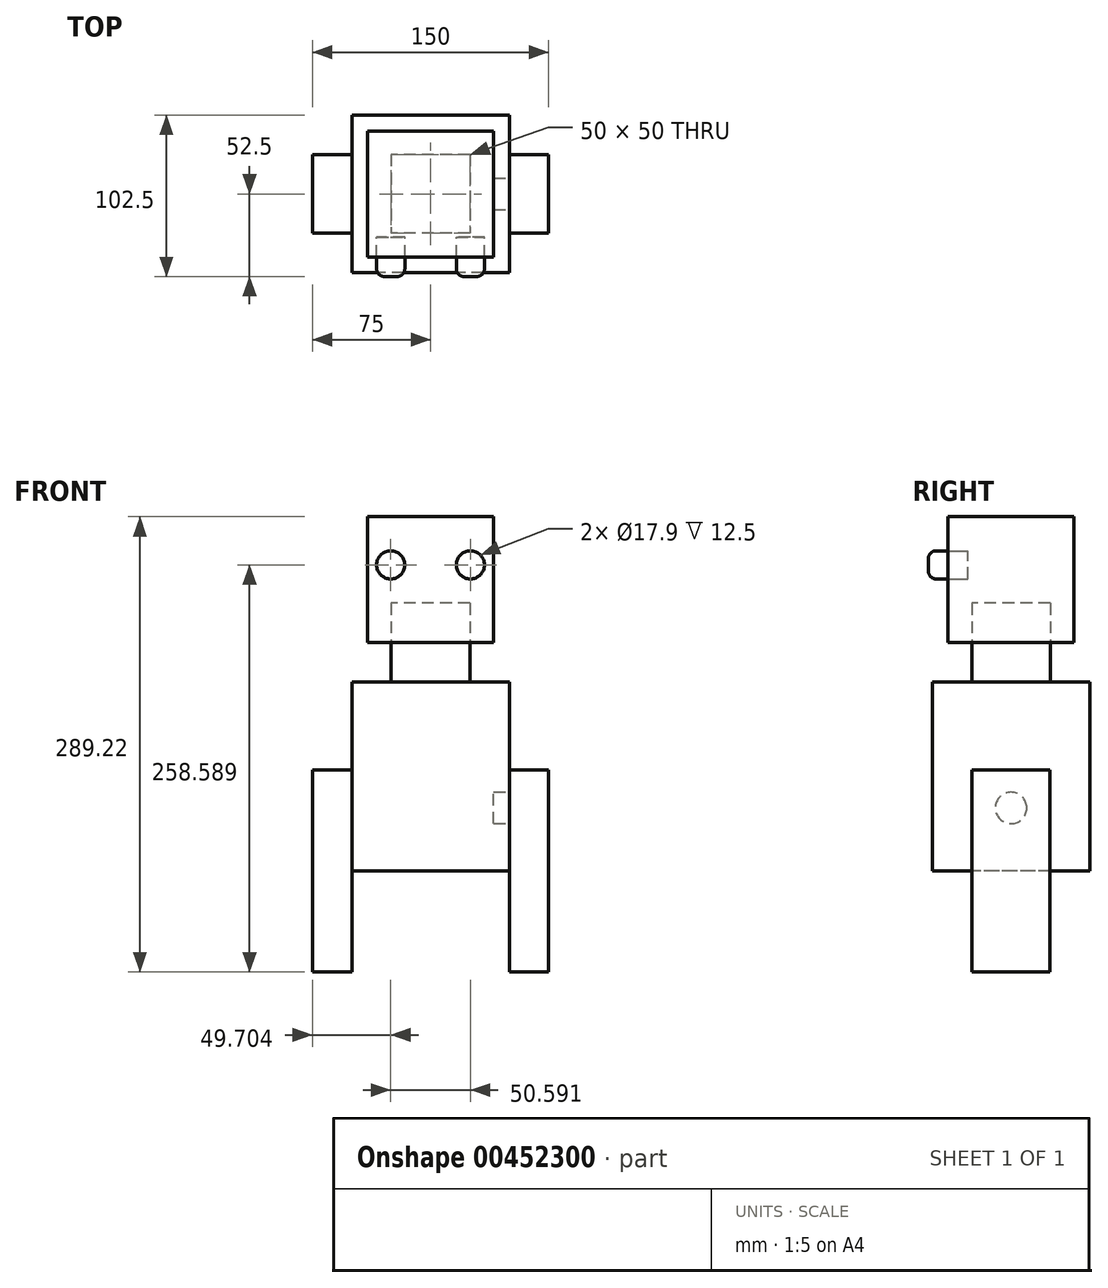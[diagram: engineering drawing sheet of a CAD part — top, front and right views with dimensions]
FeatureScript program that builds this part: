
annotation { "Feature Type Name" : "Feature", "Feature Type Description" : "" }
export const myFeature = defineFeature(function(context is Context, id is Id, definition is map)
    precondition{}
    {
        {
            var Q0;
            Q0=qCreatedBy(makeId("Top.planeOp"),FACE);
            var sketch = newSketch(context, id + "F0", { "sketchPlane" : qUnion([Q0])});
            skLineSegment(sketch, "E0.bottom", {"start": v(50, 50) * mm, "end": v(-50, 50) * mm});
            skLineSegment(sketch, "E0.top", {"start": v(50, -50) * mm, "end": v(-50, -50) * mm});
            skLineSegment(sketch, "E0.left", {"start": v(50, 50) * mm, "end": v(50, -50) * mm});
            skLineSegment(sketch, "E0.right", {"start": v(-50, 50) * mm, "end": v(-50, -50) * mm});
            skPoint(sketch, "E0.middle", {"position": v(0, 0) * mm});
            skSolve(sketch);
        }
        {
            var Q0;
            Q0=makeQuery(id+"F0.imprint","IMPRINT",FACE,{"disambiguationData":[TD([[makeQuery(id+"F0.imprint","IMPRINT",EDGE,{"derivedFrom":sQuery(id+"F0.wireOp",EDGE,"E0.bottom")}),1.0]])]});
            extrude(context, id + "F1", {"entities" : qUnion([Q0]), "depth" : 120 * mm});
        }
        {
            var Q0;
            Q0=makeQuery(id+"F1.opExtrude","CAP_FACE",FACE,{"disambiguationData":[OSD([sQuery(id+"F0.wireOp",EDGE,"E0.bottom"),sQuery(id+"F0.wireOp",EDGE,"E0.top"),sQuery(id+"F0.wireOp",EDGE,"E0.left"),sQuery(id+"F0.wireOp",EDGE,"E0.right")])],"isStart":false});
            var sketch = newSketch(context, id + "F2", { "sketchPlane" : qUnion([Q0])});
            skLineSegment(sketch, "E1.bottom", {"start": v(25, 25) * mm, "end": v(-25, 25) * mm});
            skLineSegment(sketch, "E1.top", {"start": v(25, -25) * mm, "end": v(-25, -25) * mm});
            skLineSegment(sketch, "E1.left", {"start": v(25, 25) * mm, "end": v(25, -25) * mm});
            skLineSegment(sketch, "E1.right", {"start": v(-25, 25) * mm, "end": v(-25, -25) * mm});
            skPoint(sketch, "E1.middle", {"position": v(0, 0) * mm});
            skSolve(sketch);
        }
        {
            var Q0;
            Q0=makeQuery(id+"F2.imprint","IMPRINT",FACE,{"disambiguationData":[TD([[makeQuery(id+"F2.imprint","IMPRINT",EDGE,{"derivedFrom":sQuery(id+"F2.wireOp",EDGE,"E1.bottom")}),1.0]])]});
            extrude(context, id + "F3", {"entities" : qUnion([Q0]), "operationType" : NewBodyOperationType.ADD, "depth" : 50 * mm});
        }
        {
            var Q0;
            Q0=qCreatedBy(makeId("Top.planeOp"),FACE);
            cPlane(context, id + "F4", {"entities" : qUnion([Q0]), "cplaneType" : CPlaneType.OFFSET, "offset" : 145 * mm, "width" : 150 * mm, "height" : 150 * mm});
        }
        {
            var Q0;
            Q0=qCreatedBy(id+"F4.planeOp",FACE);
            var sketch = newSketch(context, id + "F5", { "sketchPlane" : qUnion([Q0])});
            skLineSegment(sketch, "E2.bottom", {"start": v(-40, -40) * mm, "end": v(40, -40) * mm});
            skLineSegment(sketch, "E2.top", {"start": v(-40, 40) * mm, "end": v(40, 40) * mm});
            skLineSegment(sketch, "E2.left", {"start": v(-40, -40) * mm, "end": v(-40, 40) * mm});
            skLineSegment(sketch, "E2.right", {"start": v(40, -40) * mm, "end": v(40, 40) * mm});
            skPoint(sketch, "E2.middle", {"position": v(0, 0) * mm});
            skSolve(sketch);
        }
        {
            var Q0;
            Q0=makeQuery(id+"F5.imprint","IMPRINT",FACE,{"disambiguationData":[TD([[makeQuery(id+"F5.imprint","IMPRINT",EDGE,{"derivedFrom":sQuery(id+"F5.wireOp",EDGE,"E2.bottom")}),1.0]])]});
            extrude(context, id + "F6", {"entities" : qUnion([Q0]), "depth" : 80 * mm});
        }
        {
            var Q0;
            Q0=makeQuery(id+"F1.opExtrude","SWEPT_BODY",BODY,{"disambiguationData":[OSD([sQuery(id+"F0.wireOp",EDGE,"E0.bottom"),sQuery(id+"F0.wireOp",EDGE,"E0.top"),sQuery(id+"F0.wireOp",EDGE,"E0.left"),sQuery(id+"F0.wireOp",EDGE,"E0.right")])]});
            var Q1;
            Q1=makeQuery(id+"F6.opExtrude","SWEPT_BODY",BODY,{"disambiguationData":[OSD([sQuery(id+"F5.wireOp",EDGE,"E2.bottom"),sQuery(id+"F5.wireOp",EDGE,"E2.top"),sQuery(id+"F5.wireOp",EDGE,"E2.left"),sQuery(id+"F5.wireOp",EDGE,"E2.right")])]});
            booleanBodies(context, id + "F7", {"operationType" : BooleanOperationType.SUBTRACTION, "tools" : qUnion([Q0]), "targets" : qUnion([Q1]), "keepTools" : true});
        }
        {
            var Q0;
            Q0=makeQuery(id+"F1.opExtrude","SWEPT_FACE",FACE,{"disambiguationData":[OSD([sQuery(id+"F0.wireOp",EDGE,"E0.left")])]});
            var sketch = newSketch(context, id + "F8", { "sketchPlane" : qUnion([Q0])});
            skLineSegment(sketch, "E3", {"start": v(0, 0) * mm, "end": v(0, 40) * mm});
            skCircle(sketch, "E4", {"center": v(0, 40) * mm, "radius": 10 * mm});
            skSolve(sketch);
        }
        {
            var Q0;
            Q0=makeQuery(id+"F8.imprint","IMPRINT",FACE,{"disambiguationData":[TD([[makeQuery(id+"F8.imprint","IMPRINT",EDGE,{"derivedFrom":sQuery(id+"F8.wireOp",EDGE,"E4")}),1.0]])]});
            extrude(context, id + "F9", {"entities" : qUnion([Q0]), "oppositeDirection" : true, "depth" : 10 * mm});
        }
        {
            var Q0;
            Q0=makeQuery(id+"F1.opExtrude","SWEPT_FACE",FACE,{"disambiguationData":[OSD([sQuery(id+"F0.wireOp",EDGE,"E0.left")])]});
            var sketch = newSketch(context, id + "F10", { "sketchPlane" : qUnion([Q0])});
            skLineSegment(sketch, "E5.bottom", {"start": v(24.83, 64.22) * mm, "end": v(-24.83, 64.22) * mm});
            skLineSegment(sketch, "E5.top", {"start": v(24.83, -64.22) * mm, "end": v(-24.83, -64.22) * mm});
            skLineSegment(sketch, "E5.left", {"start": v(24.83, 64.22) * mm, "end": v(24.83, -64.22) * mm});
            skLineSegment(sketch, "E5.right", {"start": v(-24.83, 64.22) * mm, "end": v(-24.83, -64.22) * mm});
            skPoint(sketch, "E5.middle", {"position": v(0, 0) * mm});
            skSolve(sketch);
        }
        {
            var Q0;
            {var subQ0=sQuery(id+"F10.wireOp",EDGE,"E5.bottom");Q0=makeQuery(id+"F10.imprint","IMPRINT",FACE,{"disambiguationData":[TD([[makeQuery(id+"F10.imprint","IMPRINT",EDGE,{"derivedFrom":subQ0}),1.0]])]});}
            var Q1;
            {var subQ0=sQuery(id+"F10.wireOp",EDGE,"E5.top");Q1=makeQuery(id+"F10.imprint","IMPRINT",FACE,{"disambiguationData":[TD([[makeQuery(id+"F10.imprint","IMPRINT",EDGE,{"derivedFrom":subQ0}),-1.0]])]});}
            extrude(context, id + "F11", {"entities" : qUnion([Q0, Q1]), "depth" : 25 * mm});
        }
        {
            var Q0;
            Q0=makeQuery(id+"F11.opExtrude","SWEPT_BODY",BODY,{"disambiguationData":[OSD([sQuery(id+"F10.wireOp",EDGE,"E5.bottom"),sQuery(id+"F10.wireOp",EDGE,"E5.top"),sQuery(id+"F10.wireOp",EDGE,"E5.left"),sQuery(id+"F10.wireOp",EDGE,"E5.right")])]});
            var Q1;
            Q1=makeQuery(id+"F1.opExtrude","SWEPT_BODY",BODY,{"disambiguationData":[OSD([sQuery(id+"F0.wireOp",EDGE,"E0.bottom"),sQuery(id+"F0.wireOp",EDGE,"E0.top"),sQuery(id+"F0.wireOp",EDGE,"E0.left"),sQuery(id+"F0.wireOp",EDGE,"E0.right")])]});
            booleanBodies(context, id + "F12", {"operationType" : BooleanOperationType.SUBTRACTION, "tools" : qUnion([Q0]), "targets" : qUnion([Q1]), "keepTools" : true});
        }
        {
            var Q0;
            Q0=makeQuery(id+"F11.opExtrude","SWEPT_BODY",BODY,{"disambiguationData":[OSD([sQuery(id+"F10.wireOp",EDGE,"E5.bottom"),sQuery(id+"F10.wireOp",EDGE,"E5.top"),sQuery(id+"F10.wireOp",EDGE,"E5.left"),sQuery(id+"F10.wireOp",EDGE,"E5.right")])]});
            var Q1;
            Q1=qCreatedBy(makeId("Right.planeOp"),FACE);
            mirror(context, id + "F13", {"entities" : qUnion([Q0]), "mirrorPlane" : qUnion([Q1])});
        }
        {
            var Q0;
            Q0=makeQuery(id+"F13.opPattern","COPY",BODY,{"derivedFrom":makeQuery(id+"F11.opExtrude","SWEPT_BODY",BODY,{"disambiguationData":[OSD([sQuery(id+"F10.wireOp",EDGE,"E5.bottom"),sQuery(id+"F10.wireOp",EDGE,"E5.top"),sQuery(id+"F10.wireOp",EDGE,"E5.left"),sQuery(id+"F10.wireOp",EDGE,"E5.right")])]}),"instanceName":"1"});
            var Q1;
            Q1=makeQuery(id+"F1.opExtrude","SWEPT_BODY",BODY,{"disambiguationData":[OSD([sQuery(id+"F0.wireOp",EDGE,"E0.bottom"),sQuery(id+"F0.wireOp",EDGE,"E0.top"),sQuery(id+"F0.wireOp",EDGE,"E0.left"),sQuery(id+"F0.wireOp",EDGE,"E0.right")])]});
            booleanBodies(context, id + "F14", {"operationType" : BooleanOperationType.SUBTRACTION, "tools" : qUnion([Q0]), "targets" : qUnion([Q1]), "keepTools" : true});
        }
        {
            var Q0;
            Q0=makeQuery(id+"F6.opExtrude","SWEPT_FACE",FACE,{"disambiguationData":[OSD([sQuery(id+"F5.wireOp",EDGE,"E2.bottom")])]});
            var sketch = newSketch(context, id + "F15", { "sketchPlane" : qUnion([Q0])});
            skCircle(sketch, "E6", {"center": v(-25.3, 194.37) * mm, "radius": 8.95 * mm});
            skSolve(sketch);
        }
        {
            var Q0;
            Q0=makeQuery(id+"F15.imprint","IMPRINT",FACE,{"disambiguationData":[TD([[makeQuery(id+"F15.imprint","IMPRINT",EDGE,{"derivedFrom":sQuery(id+"F15.wireOp",EDGE,"E6")}),1.0]])]});
            extrude(context, id + "F16", {"entities" : qUnion([Q0]), "endBound" : BoundingType.SYMMETRIC, "depth" : 25 * mm});
        }
        {
            var Q0;
            Q0=makeQuery(id+"F16.opExtrude","SWEPT_BODY",BODY,{"disambiguationData":[OSD([sQuery(id+"F15.wireOp",EDGE,"E6")])]});
            var Q1;
            Q1=qCreatedBy(makeId("Right.planeOp"),FACE);
            mirror(context, id + "F17", {"entities" : qUnion([Q0]), "mirrorPlane" : qUnion([Q1])});
        }
        {
            var Q0;
            Q0=makeQuery(id+"F16.opExtrude","SWEPT_BODY",BODY,{"disambiguationData":[OSD([sQuery(id+"F15.wireOp",EDGE,"E6")])]});
            var Q1;
            Q1=makeQuery(id+"F17.opPattern","COPY",BODY,{"derivedFrom":makeQuery(id+"F16.opExtrude","SWEPT_BODY",BODY,{"disambiguationData":[OSD([sQuery(id+"F15.wireOp",EDGE,"E6")])]}),"instanceName":"1"});
            var Q2;
            Q2=makeQuery(id+"F6.opExtrude","SWEPT_BODY",BODY,{"disambiguationData":[OSD([sQuery(id+"F5.wireOp",EDGE,"E2.bottom"),sQuery(id+"F5.wireOp",EDGE,"E2.top"),sQuery(id+"F5.wireOp",EDGE,"E2.left"),sQuery(id+"F5.wireOp",EDGE,"E2.right")])]});
            booleanBodies(context, id + "F18", {"operationType" : BooleanOperationType.SUBTRACTION, "tools" : qUnion([Q0, Q1]), "targets" : qUnion([Q2]), "keepTools" : true});
        }
        {
            var Q0;
            Q0=makeQuery(id+"F16.opExtrude","CAP_EDGE",EDGE,{"disambiguationData":[OSD([sQuery(id+"F15.wireOp",EDGE,"E6")])],"isStart":false});
            var Q1;
            Q1=makeQuery(id+"F17.opPattern","COPY",EDGE,{"derivedFrom":makeQuery(id+"F16.opExtrude","CAP_EDGE",EDGE,{"disambiguationData":[OSD([sQuery(id+"F15.wireOp",EDGE,"E6")])],"isStart":false}),"instanceName":"1"});
            fillet(context, id + "F19", {"entities" : qUnion([Q0, Q1]), "radius" : 5 * mm, "tangentPropagation" : true, "allowEdgeOverflow" : false});
        }
    });
